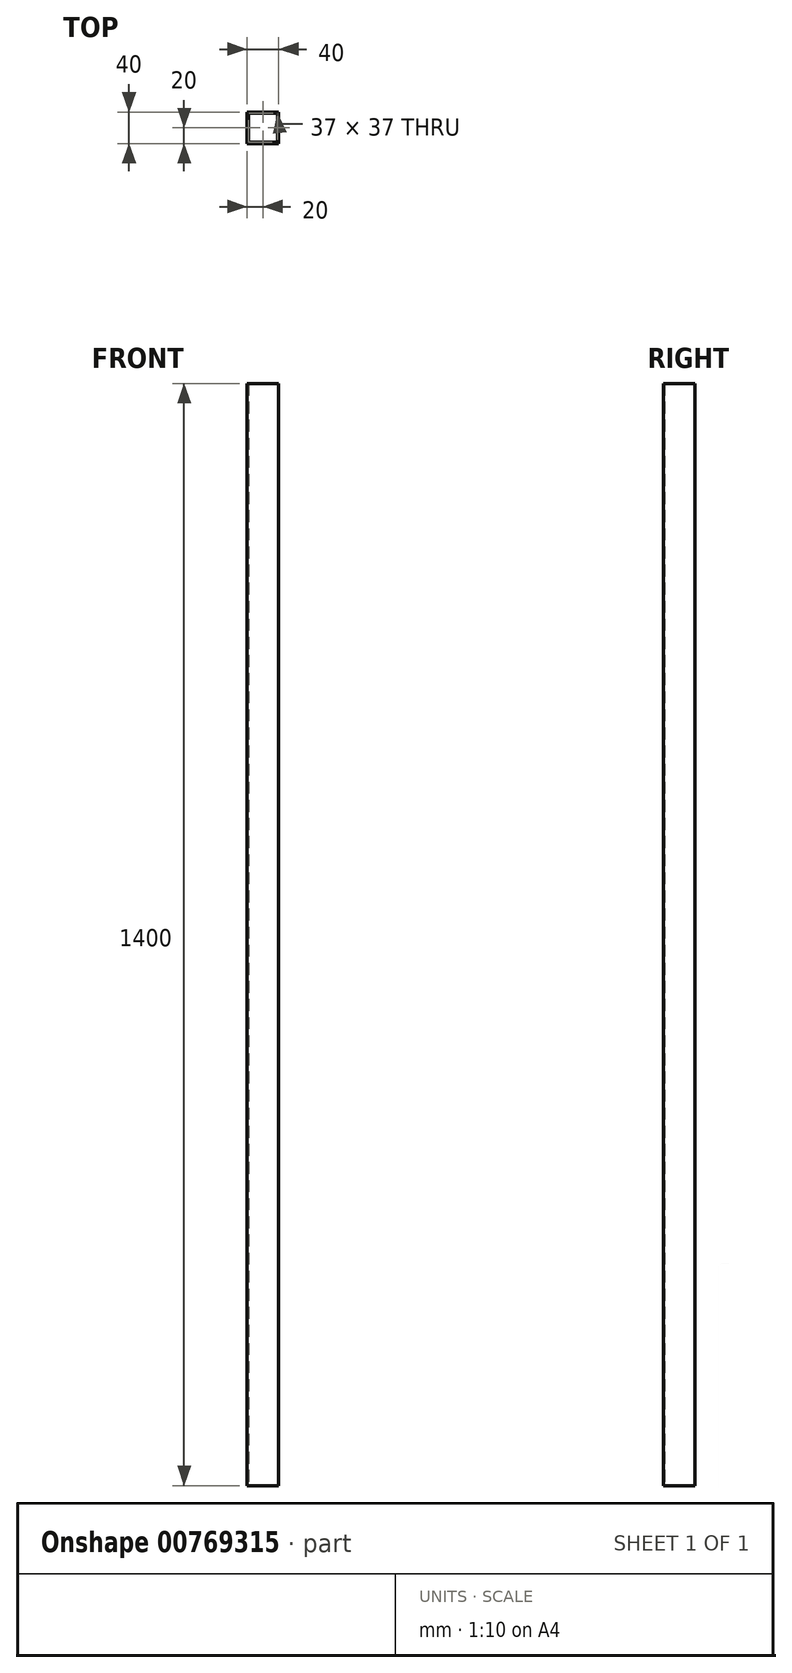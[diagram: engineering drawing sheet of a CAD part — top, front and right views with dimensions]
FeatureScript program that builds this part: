
annotation { "Feature Type Name" : "Feature", "Feature Type Description" : "" }
export const myFeature = defineFeature(function(context is Context, id is Id, definition is map)
    precondition{}
    {
        {
            var Q0;
            Q0=qCreatedBy(makeId("Top.planeOp"),FACE);
            var sketch = newSketch(context, id + "F0", { "sketchPlane" : qUnion([Q0])});
            skLineSegment(sketch, "E0.bottom", {"start": v(20, 20) * mm, "end": v(-20, 20) * mm});
            skLineSegment(sketch, "E0.top", {"start": v(20, -20) * mm, "end": v(-20, -20) * mm});
            skLineSegment(sketch, "E0.left", {"start": v(20, 20) * mm, "end": v(20, -20) * mm});
            skLineSegment(sketch, "E0.right", {"start": v(-20, 20) * mm, "end": v(-20, -20) * mm});
            skPoint(sketch, "E0.middle", {"position": v(0, 0) * mm});
            skLineSegment(sketch, "E1.bottom", {"start": v(18.5, 18.5) * mm, "end": v(-18.5, 18.5) * mm});
            skLineSegment(sketch, "E1.top", {"start": v(18.5, -18.5) * mm, "end": v(-18.5, -18.5) * mm});
            skLineSegment(sketch, "E1.left", {"start": v(18.5, 18.5) * mm, "end": v(18.5, -18.5) * mm});
            skLineSegment(sketch, "E1.right", {"start": v(-18.5, 18.5) * mm, "end": v(-18.5, -18.5) * mm});
            skSolve(sketch);
        }
        {
            var Q0;
            Q0=makeQuery(id+"F0.imprint","IMPRINT",FACE,{"disambiguationData":[TD([[makeQuery(id+"F0.imprint","IMPRINT",EDGE,{"derivedFrom":sQuery(id+"F0.wireOp",EDGE,"E0.bottom")}),1.0]])]});
            extrude(context, id + "F1", {"entities" : qUnion([Q0]), "depth" : 1400 * mm, "offsetDistance" : 25 * mm});
        }
    });
